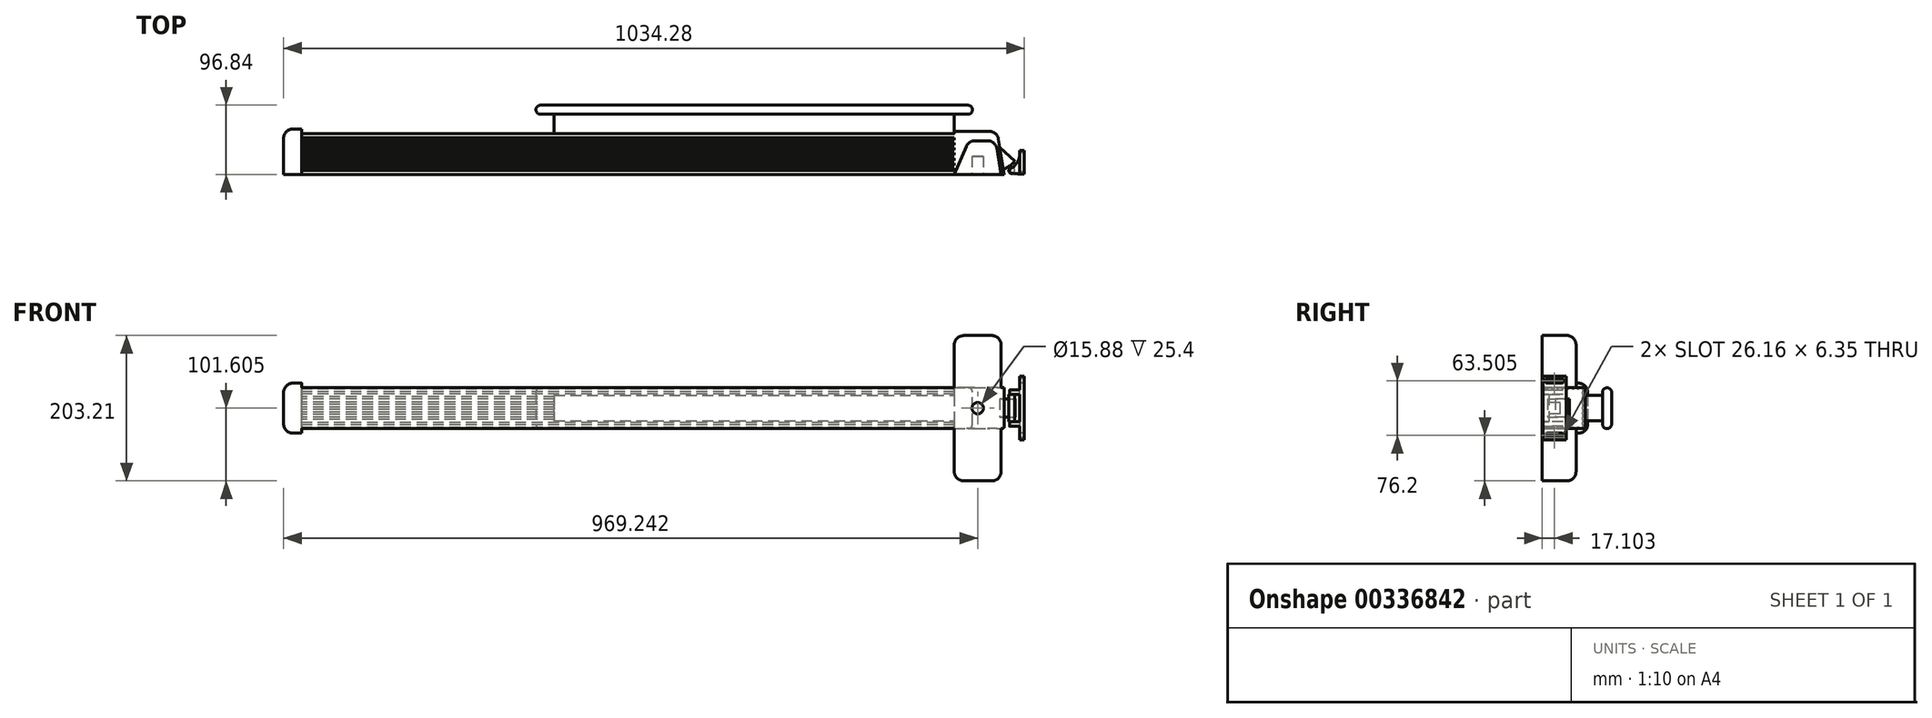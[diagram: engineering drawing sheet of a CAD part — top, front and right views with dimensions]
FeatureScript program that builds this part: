
annotation { "Feature Type Name" : "Feature", "Feature Type Description" : "" }
export const myFeature = defineFeature(function(context is Context, id is Id, definition is map)
    precondition{}
    {
        {
            var Q0;
            Q0=qCreatedBy(makeId("Front.planeOp"),FACE);
            var sketch = newSketch(context, id + "F0", { "sketchPlane" : qUnion([Q0])});
            skLineSegment(sketch, "E0.bottom", {"start": v(0, 0) * mm, "end": v(-911.23, 0) * mm});
            skLineSegment(sketch, "E0.top", {"start": v(0, 57.15) * mm, "end": v(-911.23, 57.15) * mm});
            skLineSegment(sketch, "E0.left", {"start": v(0, 0) * mm, "end": v(0, 57.15) * mm});
            skLineSegment(sketch, "E0.right", {"start": v(-911.23, 0) * mm, "end": v(-911.23, 57.15) * mm});
            skSolve(sketch);
        }
        {
            var Q0;
            Q0 = qSketchRegion(id + "F0", true);
            extrude(context, id + "F1", {"entities" : qUnion([Q0]), "oppositeDirection" : true, "depth" : 57.15 * mm});
        }
        {
            var Q0;
            Q0=qCreatedBy(makeId("Top.planeOp"),FACE);
            var sketch = newSketch(context, id + "F2", { "sketchPlane" : qUnion([Q0])});
            skLineSegment(sketch, "E1.bottom", {"start": v(0, 0) * mm, "end": v(69.85, 0) * mm});
            skLineSegment(sketch, "E1.left", {"start": v(0, 0) * mm, "end": v(0, 60.32) * mm});
            skLineSegment(sketch, "E2", {"start": v(0, 60.32) * mm, "end": v(49.18, 60.32) * mm});
            skLineSegment(sketch, "E3", {"start": v(61.72, 49.68) * mm, "end": v(69.85, 0) * mm});
            skPoint(sketch, "E4.visualSharp", {"position": v(59.97, 60.32) * mm});
            skArc(sketch, "E4.filletArc", {"start": v(61.72, 49.68) * mm, "mid": v(57.4, 57.3) * mm, "end": v(49.18, 60.33) * mm});
            skSolve(sketch);
        }
        {
            var Q0;
            Q0 = qSketchRegion(id + "F2", true);
            var Q1;
            Q1=makeQuery(id+"F1.opExtrude","SWEPT_FACE",FACE,{"disambiguationData":[OSD([sQuery(id+"F0.wireOp",EDGE,"E0.top")])]});
            extrude(context, id + "F3", {"entities" : qUnion([Q0]), "operationType" : NewBodyOperationType.ADD, "endBound" : BoundingType.UP_TO_SURFACE, "endBoundEntityFace" : qUnion([Q1]), "depth" : 25.4 * mm});
        }
        {
            var Q0;
            Q0=qCreatedBy(makeId("Top.planeOp"),FACE);
            var sketch = newSketch(context, id + "F4", { "sketchPlane" : qUnion([Q0])});
            skLineSegment(sketch, "E5", {"start": v(65.24, 0) * mm, "end": v(59.26, 36.55) * mm});
            skLineSegment(sketch, "E6", {"start": v(46.73, 47.2) * mm, "end": v(28.53, 47.2) * mm});
            skLineSegment(sketch, "E7", {"start": v(16.85, 39.48) * mm, "end": v(0, 0) * mm});
            skLineSegment(sketch, "E8", {"start": v(0, 0) * mm, "end": v(65.24, 0) * mm});
            skPoint(sketch, "E9.visualSharp", {"position": v(57.52, 47.2) * mm});
            skArc(sketch, "E9.filletArc", {"start": v(59.26, 36.55) * mm, "mid": v(54.95, 44.18) * mm, "end": v(46.73, 47.2) * mm});
            skPoint(sketch, "E10.visualSharp", {"position": v(20.14, 47.2) * mm});
            skArc(sketch, "E10.filletArc", {"start": v(28.53, 47.2) * mm, "mid": v(21.53, 45.1) * mm, "end": v(16.85, 39.48) * mm});
            skSolve(sketch);
        }
        {
            var Q0;
            Q0=makeQuery(id+"F3.opExtrude","CAP_EDGE",EDGE,{"disambiguationData":[OSD([sQuery(id+"F2.wireOp",EDGE,"E2")])],"isStart":true});
            var Q1;
            Q1=makeQuery(id+"F3.opExtrude","TWEAK_EDGE",EDGE,{"derivedFrom":[makeQuery(id+"F1.opExtrude","SWEPT_FACE",FACE,{"disambiguationData":[OSD([sQuery(id+"F0.wireOp",EDGE,"E0.top")])]}),makeQuery(id+"F2.imprint","IMPRINT",EDGE,{"derivedFrom":sQuery(id+"F2.wireOp",EDGE,"E2")})]});
            fillet(context, id + "F5", {"entities" : qUnion([Q0, Q1]), "radius" : 3.17 * mm, "tangentPropagation" : true, "allowEdgeOverflow" : false});
        }
        {
            var Q0;
            Q0 = qSketchRegion(id + "F4", true);
            extrude(context, id + "F6", {"entities" : qUnion([Q0]), "operationType" : NewBodyOperationType.ADD, "depth" : 130.17 * mm, "hasSecondDirection" : true, "secondDirectionOppositeDirection" : true, "secondDirectionDepth" : 73.02 * mm});
        }
        {
            var Q0;
            Q0=makeQuery(id+"F6.opExtrude","CAP_EDGE",EDGE,{"disambiguationData":[OSD([sQuery(id+"F4.wireOp",EDGE,"E7")])],"isStart":false});
            var Q1;
            Q1=makeQuery(id+"F6.opExtrude","CAP_EDGE",EDGE,{"disambiguationData":[OSD([sQuery(id+"F4.wireOp",EDGE,"E7")])],"isStart":true});
            fillet(context, id + "F7", {"entities" : qUnion([Q0, Q1]), "radius" : 12.7 * mm, "tangentPropagation" : true, "allowEdgeOverflow" : false});
        }
        {
            var Q0;
            Q0=makeQuery(id+"F1.opExtrude","SWEPT_FACE",FACE,{"disambiguationData":[OSD([sQuery(id+"F0.wireOp",EDGE,"E0.right")])]});
            var sketch = newSketch(context, id + "F8", { "sketchPlane" : qUnion([Q0])});
            skArc(sketch, "E11", {"start": v(-48.42, 0) * mm, "mid": v(-50, 1.59) * mm, "end": v(-51.6, 0) * mm});
            skArc(sketch, "E12.1.0.0", {"start": v(-41.28, 0) * mm, "mid": v(-42.86, 1.59) * mm, "end": v(-44.45, 0) * mm});
            skArc(sketch, "E12.2.0.0", {"start": v(-34.13, 0) * mm, "mid": v(-35.72, 1.59) * mm, "end": v(-37.3, 0) * mm});
            skArc(sketch, "E12.3.0.0", {"start": v(-26.99, 0) * mm, "mid": v(-28.57, 1.59) * mm, "end": v(-30.16, 0) * mm});
            skArc(sketch, "E12.4.0.0", {"start": v(-19.84, 0) * mm, "mid": v(-21.43, 1.59) * mm, "end": v(-23.02, 0) * mm});
            skArc(sketch, "E12.5.0.0", {"start": v(-12.7, 0) * mm, "mid": v(-14.29, 1.59) * mm, "end": v(-15.87, 0) * mm});
            skArc(sketch, "E12.6.0.0", {"start": v(-5.56, 0) * mm, "mid": v(-7.14, 1.59) * mm, "end": v(-8.73, 0) * mm});
            skLineSegment(sketch, "E12.direction1", {"start": v(-51.6, 0) * mm, "end": v(-44.45, 0) * mm, "construction": true});
            skLineSegment(sketch, "E13", {"start": v(-50, 7.14) * mm, "end": v(-57.15, 7.14) * mm, "construction": true});
            skPoint(sketch, "E13.startSnap0", {"position": v(-50, 1.59) * mm});
            skLineSegment(sketch, "E14", {"start": v(-50, 7.14) * mm, "end": v(-50, 0) * mm, "construction": true});
            skLineSegment(sketch, "E15.0", {"start": v(-57.15, 0) * mm, "end": v(-57.15, 57.15) * mm, "construction": true});
            skLineSegment(sketch, "E16", {"start": v(-57.15, 28.58) * mm, "end": v(0, 28.58) * mm, "construction": true});
            skArc(sketch, "E17.1.0", {"start": v(-57.15, 5.56) * mm, "mid": v(-55.56, 7.14) * mm, "end": v(-57.15, 8.73) * mm});
            skPoint(sketch, "E17.center", {"position": v(-50, 7.14) * mm});
            skLineSegment(sketch, "E17.anchor1", {"start": v(-50, 7.14) * mm, "end": v(-51.6, 0) * mm, "construction": true});
            skLineSegment(sketch, "E17.anchor2", {"start": v(-50, 7.14) * mm, "end": v(-57.15, 8.73) * mm, "construction": true});
            skArc(sketch, "E18.MirrorCS", {"start": v(-48.42, 57.15) * mm, "mid": v(-50, 55.56) * mm, "end": v(-51.6, 57.15) * mm});
            skPoint(sketch, "E19.MirrorP", {"position": v(-50, 55.56) * mm});
            skArc(sketch, "E20.MirrorCS", {"start": v(-34.13, 57.15) * mm, "mid": v(-35.72, 55.56) * mm, "end": v(-37.3, 57.15) * mm});
            skArc(sketch, "E21.MirrorCS", {"start": v(-41.28, 57.15) * mm, "mid": v(-42.86, 55.56) * mm, "end": v(-44.45, 57.15) * mm});
            skArc(sketch, "E22.MirrorCS", {"start": v(-26.99, 57.15) * mm, "mid": v(-28.57, 55.56) * mm, "end": v(-30.16, 57.15) * mm});
            skArc(sketch, "E23.MirrorCS", {"start": v(-5.56, 57.15) * mm, "mid": v(-7.14, 55.56) * mm, "end": v(-8.73, 57.15) * mm});
            skLineSegment(sketch, "E24.MirrorCS", {"start": v(-51.6, 57.15) * mm, "end": v(-44.45, 57.15) * mm, "construction": true});
            skArc(sketch, "E25.MirrorCS", {"start": v(-19.84, 57.15) * mm, "mid": v(-21.43, 55.56) * mm, "end": v(-23.02, 57.15) * mm});
            skArc(sketch, "E26.MirrorCS", {"start": v(-12.7, 57.15) * mm, "mid": v(-14.29, 55.56) * mm, "end": v(-15.87, 57.15) * mm});
            skLineSegment(sketch, "E27", {"start": v(-51.6, 0) * mm, "end": v(-48.42, 0) * mm});
            skLineSegment(sketch, "E28", {"start": v(-44.45, 0) * mm, "end": v(-41.28, 0) * mm});
            skLineSegment(sketch, "E29", {"start": v(-37.3, 0) * mm, "end": v(-34.13, 0) * mm});
            skLineSegment(sketch, "E30", {"start": v(-30.16, 0) * mm, "end": v(-26.99, 0) * mm});
            skLineSegment(sketch, "E31", {"start": v(-23.02, 0) * mm, "end": v(-19.84, 0) * mm});
            skLineSegment(sketch, "E32", {"start": v(-15.87, 0) * mm, "end": v(-12.7, 0) * mm});
            skLineSegment(sketch, "E33", {"start": v(-8.73, 0) * mm, "end": v(-5.56, 0) * mm});
            skLineSegment(sketch, "E34", {"start": v(-5.56, 57.15) * mm, "end": v(-8.73, 57.15) * mm});
            skLineSegment(sketch, "E35", {"start": v(-12.7, 57.15) * mm, "end": v(-15.87, 57.15) * mm});
            skLineSegment(sketch, "E36", {"start": v(-19.84, 57.15) * mm, "end": v(-23.02, 57.15) * mm});
            skLineSegment(sketch, "E37", {"start": v(-26.99, 57.15) * mm, "end": v(-30.16, 57.15) * mm});
            skLineSegment(sketch, "E38", {"start": v(-34.13, 57.15) * mm, "end": v(-37.3, 57.15) * mm});
            skLineSegment(sketch, "E39", {"start": v(-41.28, 57.15) * mm, "end": v(-44.45, 57.15) * mm});
            skLineSegment(sketch, "E40", {"start": v(-48.42, 57.15) * mm, "end": v(-51.6, 57.15) * mm});
            skLineSegment(sketch, "E41", {"start": v(-57.15, 5.56) * mm, "end": v(-57.15, 8.73) * mm});
            skArc(sketch, "E42.0.1.0", {"start": v(-57.15, 12.7) * mm, "mid": v(-55.56, 14.29) * mm, "end": v(-57.15, 15.88) * mm});
            skLineSegment(sketch, "E42.0.1.1", {"start": v(-57.15, 12.7) * mm, "end": v(-57.15, 15.88) * mm});
            skArc(sketch, "E42.0.2.0", {"start": v(-57.15, 19.84) * mm, "mid": v(-55.56, 21.43) * mm, "end": v(-57.15, 23.02) * mm});
            skLineSegment(sketch, "E42.0.2.1", {"start": v(-57.15, 19.84) * mm, "end": v(-57.15, 23.02) * mm});
            skArc(sketch, "E42.0.3.0", {"start": v(-57.15, 26.99) * mm, "mid": v(-55.56, 28.58) * mm, "end": v(-57.15, 30.16) * mm});
            skLineSegment(sketch, "E42.0.3.1", {"start": v(-57.15, 26.99) * mm, "end": v(-57.15, 30.16) * mm});
            skArc(sketch, "E42.0.4.0", {"start": v(-57.15, 34.13) * mm, "mid": v(-55.56, 35.72) * mm, "end": v(-57.15, 37.3) * mm});
            skLineSegment(sketch, "E42.0.4.1", {"start": v(-57.15, 34.13) * mm, "end": v(-57.15, 37.3) * mm});
            skArc(sketch, "E42.0.5.0", {"start": v(-57.15, 41.28) * mm, "mid": v(-55.56, 42.86) * mm, "end": v(-57.15, 44.45) * mm});
            skLineSegment(sketch, "E42.0.5.1", {"start": v(-57.15, 41.28) * mm, "end": v(-57.15, 44.45) * mm});
            skArc(sketch, "E42.0.6.0", {"start": v(-57.15, 48.42) * mm, "mid": v(-55.56, 50) * mm, "end": v(-57.15, 51.6) * mm});
            skLineSegment(sketch, "E42.0.6.1", {"start": v(-57.15, 48.42) * mm, "end": v(-57.15, 51.6) * mm});
            skLineSegment(sketch, "E42.direction1", {"start": v(-57.15, 5.56) * mm, "end": v(-31.75, 5.56) * mm, "construction": true});
            skLineSegment(sketch, "E42.direction2", {"start": v(-57.15, 5.56) * mm, "end": v(-57.15, 12.7) * mm, "construction": true});
            skSolve(sketch);
        }
        {
            var Q0;
            Q0 = qSketchRegion(id + "F8", true);
            var Q1;
            Q1=makeQuery(id+"F3.opExtrude","SWEPT_FACE",FACE,{"disambiguationData":[OSD([sQuery(id+"F2.wireOp",EDGE,"E1.left")])]});
            extrude(context, id + "F9", {"entities" : qUnion([Q0]), "operationType" : NewBodyOperationType.REMOVE, "endBound" : BoundingType.UP_TO_SURFACE, "oppositeDirection" : true, "endBoundEntityFace" : qUnion([Q1]), "depth" : 25.4 * mm});
        }
        {
            var Q0;
            Q0=makeQuery(id+"F1.opExtrude","SWEPT_FACE",FACE,{"disambiguationData":[OSD([sQuery(id+"F0.wireOp",EDGE,"E0.right")])]});
            var sketch = newSketch(context, id + "F10", { "sketchPlane" : qUnion([Q0])});
            skLineSegment(sketch, "E43.bottom", {"start": v(0, 63.5) * mm, "end": v(-63.5, 63.5) * mm});
            skLineSegment(sketch, "E43.top", {"start": v(0, -6.35) * mm, "end": v(-63.5, -6.35) * mm});
            skLineSegment(sketch, "E43.left", {"start": v(0, 63.5) * mm, "end": v(0, -6.35) * mm});
            skLineSegment(sketch, "E43.right", {"start": v(-63.5, 63.5) * mm, "end": v(-63.5, -6.35) * mm});
            skSolve(sketch);
        }
        {
            var Q0;
            Q0 = qSketchRegion(id + "F10", true);
            extrude(context, id + "F11", {"entities" : qUnion([Q0]), "operationType" : NewBodyOperationType.ADD, "depth" : 25.4 * mm});
        }
        {
            var Q0;
            Q0=makeQuery(id+"F11.opExtrude","SWEPT_EDGE",EDGE,{"disambiguationData":[OSD([sQuery(id+"F10.wireOp",EDGE,"E43.top"),sQuery(id+"F10.wireOp",EDGE,"E43.right")])]});
            var Q1;
            Q1=makeQuery(id+"F11.opExtrude","SWEPT_EDGE",EDGE,{"disambiguationData":[OSD([sQuery(id+"F10.wireOp",EDGE,"E43.bottom"),sQuery(id+"F10.wireOp",EDGE,"E43.right")])]});
            fillet(context, id + "F12", {"entities" : qUnion([Q0, Q1]), "radius" : 12.7 * mm, "tangentPropagation" : true, "allowEdgeOverflow" : false});
        }
        {
            var Q0;
            Q0=makeQuery(id+"F11.opExtrude","CAP_EDGE",EDGE,{"disambiguationData":[OSD([sQuery(id+"F10.wireOp",EDGE,"E43.bottom")])],"isStart":false});
            fillet(context, id + "F13", {"entities" : qUnion([Q0]), "radius" : 12.7 * mm, "tangentPropagation" : true, "allowEdgeOverflow" : false});
        }
        {
            var Q0;
            {var subQ0=sQuery(id+"F2.wireOp",EDGE,"E1.left");var subQ1=sQuery(id+"F8.wireOp",EDGE,"E42.0.6.0");var subQ2=sQuery(id+"F0.wireOp",EDGE,"E0.top");var subQ3=sQuery(id+"F0.wireOp",EDGE,"E0.right");Q0=makeQuery(id+"F9.boolean.opBoolean","SPLIT",FACE,{"disambiguationData":[TD([makeQuery(id+"F1.opExtrude","SWEPT_FACE",FACE,{"disambiguationData":[OSD([subQ2])]}),makeQuery(id+"F1.opExtrude","SWEPT_FACE",FACE,{"disambiguationData":[OSD([subQ3])]}),makeQuery(id+"F3.opExtrude","CAP_FACE",FACE,{"disambiguationData":[OSD([subQ2])],"isStart":false}),makeQuery(id+"F3.opExtrude","SWEPT_FACE",FACE,{"disambiguationData":[OSD([subQ0])]}),makeQuery(id+"F5.opFillet","BLEND_FACE",FACE,{"disambiguationData":[OSD([subQ2,sQuery(id+"F2.wireOp",EDGE,"E2")])]}),makeQuery(id+"F9.opExtrude","SWEPT_FACE",FACE,{"disambiguationData":[OSD([subQ1])]}),makeQuery(id+"F9.opExtrude","CAP_FACE",FACE,{"disambiguationData":[OSD([subQ0]),ownerDisambiguation([makeQuery(id+"F9.opExtrude","SWEPT_BODY",BODY,{"disambiguationData":[OSD([sQuery(id+"F8.wireOp",EDGE,"E17.1.0"),sQuery(id+"F8.wireOp",EDGE,"E41")])]})])],"isStart":false}),makeQuery(id+"F9.opExtrude","CAP_FACE",FACE,{"disambiguationData":[OSD([subQ0]),ownerDisambiguation([makeQuery(id+"F9.opExtrude","SWEPT_BODY",BODY,{"disambiguationData":[OSD([sQuery(id+"F8.wireOp",EDGE,"E42.0.1.0"),sQuery(id+"F8.wireOp",EDGE,"E42.0.1.1")])]})])],"isStart":false}),makeQuery(id+"F9.opExtrude","CAP_FACE",FACE,{"disambiguationData":[OSD([subQ0]),ownerDisambiguation([makeQuery(id+"F9.opExtrude","SWEPT_BODY",BODY,{"disambiguationData":[OSD([sQuery(id+"F8.wireOp",EDGE,"E42.0.2.0"),sQuery(id+"F8.wireOp",EDGE,"E42.0.2.1")])]})])],"isStart":false}),makeQuery(id+"F9.opExtrude","CAP_FACE",FACE,{"disambiguationData":[OSD([subQ0]),ownerDisambiguation([makeQuery(id+"F9.opExtrude","SWEPT_BODY",BODY,{"disambiguationData":[OSD([sQuery(id+"F8.wireOp",EDGE,"E42.0.3.0"),sQuery(id+"F8.wireOp",EDGE,"E42.0.3.1")])]})])],"isStart":false}),makeQuery(id+"F9.opExtrude","CAP_FACE",FACE,{"disambiguationData":[OSD([subQ0]),ownerDisambiguation([makeQuery(id+"F9.opExtrude","SWEPT_BODY",BODY,{"disambiguationData":[OSD([sQuery(id+"F8.wireOp",EDGE,"E42.0.4.0"),sQuery(id+"F8.wireOp",EDGE,"E42.0.4.1")])]})])],"isStart":false}),makeQuery(id+"F9.opExtrude","CAP_FACE",FACE,{"disambiguationData":[OSD([subQ0]),ownerDisambiguation([makeQuery(id+"F9.opExtrude","SWEPT_BODY",BODY,{"disambiguationData":[OSD([sQuery(id+"F8.wireOp",EDGE,"E42.0.5.0"),sQuery(id+"F8.wireOp",EDGE,"E42.0.5.1")])]})])],"isStart":false}),makeQuery(id+"F9.opExtrude","CAP_FACE",FACE,{"disambiguationData":[OSD([subQ0]),ownerDisambiguation([makeQuery(id+"F9.opExtrude","SWEPT_BODY",BODY,{"disambiguationData":[OSD([subQ1,sQuery(id+"F8.wireOp",EDGE,"E42.0.6.1")])]})])],"isStart":false})])],"derivedFrom":makeQuery(id+"F1.opExtrude","CAP_FACE",FACE,{"disambiguationData":[OSD([sQuery(id+"F0.wireOp",EDGE,"E0.bottom"),subQ2,sQuery(id+"F0.wireOp",EDGE,"E0.left"),subQ3])],"isStart":false})});}
            var sketch = newSketch(context, id + "F14", { "sketchPlane" : qUnion([Q0])});
            skPoint(sketch, "E44.0", {"position": v(0, 46.43) * mm});
            skPoint(sketch, "E45.0", {"position": v(0, 10.72) * mm});
            skLineSegment(sketch, "E46.bottom", {"start": v(0, 46.43) * mm, "end": v(558.8, 46.43) * mm});
            skLineSegment(sketch, "E46.top", {"start": v(0, 10.72) * mm, "end": v(558.8, 10.72) * mm});
            skLineSegment(sketch, "E46.left", {"start": v(0, 46.43) * mm, "end": v(0, 10.72) * mm});
            skLineSegment(sketch, "E46.right", {"start": v(558.8, 46.43) * mm, "end": v(558.8, 10.72) * mm});
            skSolve(sketch);
        }
        {
            var Q0;
            Q0 = qSketchRegion(id + "F14", true);
            extrude(context, id + "F15", {"entities" : qUnion([Q0]), "operationType" : NewBodyOperationType.ADD, "oppositeDirection" : true, "depth" : 25.4 * mm, "hasSecondDirection" : true, "secondDirectionOppositeDirection" : false, "secondDirectionDepth" : 26.99 * mm});
        }
        {
            var Q0;
            Q0=makeQuery(id+"F15.opExtrude","CAP_FACE",FACE,{"disambiguationData":[OSD([sQuery(id+"F14.wireOp",EDGE,"E46.bottom"),sQuery(id+"F14.wireOp",EDGE,"E46.top"),sQuery(id+"F14.wireOp",EDGE,"E46.left"),sQuery(id+"F14.wireOp",EDGE,"E46.right")])],"isStart":true});
            var sketch = newSketch(context, id + "F16", { "sketchPlane" : qUnion([Q0])});
            skLineSegment(sketch, "E47.bottom", {"start": v(-25.4, 57.15) * mm, "end": v(584.2, 57.15) * mm});
            skLineSegment(sketch, "E47.top", {"start": v(-25.4, 0) * mm, "end": v(584.2, 0) * mm});
            skLineSegment(sketch, "E47.left", {"start": v(-25.4, 57.15) * mm, "end": v(-25.4, 0) * mm});
            skLineSegment(sketch, "E47.right", {"start": v(584.2, 57.15) * mm, "end": v(584.2, 0) * mm});
            skSolve(sketch);
        }
        {
            var Q0;
            Q0 = qSketchRegion(id + "F16", true);
            extrude(context, id + "F17", {"entities" : qUnion([Q0]), "operationType" : NewBodyOperationType.ADD, "depth" : 12.7 * mm});
        }
        {
            var Q0;
            Q0=makeQuery(id+"F17.opExtrude","CAP_EDGE",EDGE,{"disambiguationData":[OSD([sQuery(id+"F16.wireOp",EDGE,"E47.bottom")])],"isStart":false});
            var Q1;
            Q1=makeQuery(id+"F17.opExtrude","CAP_EDGE",EDGE,{"disambiguationData":[OSD([sQuery(id+"F16.wireOp",EDGE,"E47.left")])],"isStart":false});
            var Q2;
            Q2=makeQuery(id+"F17.opExtrude","CAP_EDGE",EDGE,{"disambiguationData":[OSD([sQuery(id+"F16.wireOp",EDGE,"E47.top")])],"isStart":false});
            var Q3;
            Q3=makeQuery(id+"F17.opExtrude","CAP_EDGE",EDGE,{"disambiguationData":[OSD([sQuery(id+"F16.wireOp",EDGE,"E47.top")])],"isStart":true});
            var Q4;
            Q4=makeQuery(id+"F17.opExtrude","CAP_EDGE",EDGE,{"disambiguationData":[OSD([sQuery(id+"F16.wireOp",EDGE,"E47.left")])],"isStart":true});
            var Q5;
            Q5=makeQuery(id+"F17.opExtrude","SWEPT_EDGE",EDGE,{"disambiguationData":[OSD([sQuery(id+"F16.wireOp",EDGE,"E47.top"),sQuery(id+"F16.wireOp",EDGE,"E47.left")])]});
            var Q6;
            Q6=makeQuery(id+"F17.opExtrude","SWEPT_EDGE",EDGE,{"disambiguationData":[OSD([sQuery(id+"F16.wireOp",EDGE,"E47.bottom"),sQuery(id+"F16.wireOp",EDGE,"E47.left")])]});
            var Q7;
            Q7=makeQuery(id+"F17.opExtrude","CAP_EDGE",EDGE,{"disambiguationData":[OSD([sQuery(id+"F16.wireOp",EDGE,"E47.right")])],"isStart":true});
            var Q8;
            Q8=makeQuery(id+"F17.opExtrude","CAP_EDGE",EDGE,{"disambiguationData":[OSD([sQuery(id+"F16.wireOp",EDGE,"E47.right")])],"isStart":false});
            var Q9;
            Q9=makeQuery(id+"F17.opExtrude","SWEPT_EDGE",EDGE,{"disambiguationData":[OSD([sQuery(id+"F16.wireOp",EDGE,"E47.top"),sQuery(id+"F16.wireOp",EDGE,"E47.right")])]});
            var Q10;
            Q10=makeQuery(id+"F17.opExtrude","SWEPT_EDGE",EDGE,{"disambiguationData":[OSD([sQuery(id+"F16.wireOp",EDGE,"E47.bottom"),sQuery(id+"F16.wireOp",EDGE,"E47.right")])]});
            var Q11;
            Q11=makeQuery(id+"F17.opExtrude","CAP_EDGE",EDGE,{"disambiguationData":[OSD([sQuery(id+"F16.wireOp",EDGE,"E47.bottom")])],"isStart":true});
            fillet(context, id + "F18", {"entities" : qUnion([Q0, Q1, Q2, Q3, Q4, Q5, Q6, Q7, Q8, Q9, Q10, Q11]), "radius" : 6.35 * mm, "tangentPropagation" : true, "allowEdgeOverflow" : false});
        }
        {
            var Q0;
            Q0=makeQuery(id+"F11.boolean.opBoolean","MERGE",FACE,{"derivedFrom":[makeQuery(id+"F6.boolean.opBoolean","MERGE",FACE,{"derivedFrom":[makeQuery(id+"F3.boolean.opBoolean","MERGE",FACE,{"derivedFrom":[makeQuery(id+"F1.opExtrude","CAP_FACE",FACE,{"disambiguationData":[OSD([sQuery(id+"F0.wireOp",EDGE,"E0.bottom"),sQuery(id+"F0.wireOp",EDGE,"E0.top"),sQuery(id+"F0.wireOp",EDGE,"E0.left"),sQuery(id+"F0.wireOp",EDGE,"E0.right")])],"isStart":true}),makeQuery(id+"F3.opExtrude","SWEPT_FACE",FACE,{"disambiguationData":[OSD([sQuery(id+"F2.wireOp",EDGE,"E1.bottom")])]})]}),makeQuery(id+"F6.opExtrude","SWEPT_FACE",FACE,{"disambiguationData":[OSD([sQuery(id+"F4.wireOp",EDGE,"E8")])]})]}),makeQuery(id+"F11.opExtrude","SWEPT_FACE",FACE,{"disambiguationData":[OSD([sQuery(id+"F10.wireOp",EDGE,"E43.left")])]})]});
            var sketch = newSketch(context, id + "F19", { "sketchPlane" : qUnion([Q0])});
            skPoint(sketch, "E48.0", {"position": v(0, 117.48) * mm});
            skPoint(sketch, "E49.0", {"position": v(65.24, -60.32) * mm});
            skLineSegment(sketch, "E50", {"start": v(0, 117.48) * mm, "end": v(65.24, -60.33) * mm, "construction": true});
            skCircle(sketch, "E51", {"center": v(32.62, 28.58) * mm, "radius": 7.94 * mm});
            skSolve(sketch);
        }
        {
            var Q0;
            Q0 = qSketchRegion(id + "F19", true);
            extrude(context, id + "F20", {"entities" : qUnion([Q0]), "operationType" : NewBodyOperationType.REMOVE, "oppositeDirection" : true, "depth" : 25.4 * mm});
        }
        {
            var Q0;
            Q0=qCreatedBy(makeId("Front.planeOp"),FACE);
            var sketch = newSketch(context, id + "F21", { "sketchPlane" : qUnion([Q0])});
            skPoint(sketch, "E52.0", {"position": v(69.85, 28.58) * mm});
            skSolve(sketch);
        }
        {
            var Q0;
            Q0=qCreatedBy(makeId("Top.planeOp"),FACE);
            var Q1;
            Q1=sQuery(id+"F21.wireOp",VERTEX,"E52.0");
            cPlane(context, id + "F22", {"entities" : qUnion([Q0, Q1]), "cplaneType" : CPlaneType.PLANE_POINT, "offset" : 25.4 * mm, "width" : 152.4 * mm, "height" : 152.4 * mm});
        }
        {
            var Q0;
            Q0=qCreatedBy(id+"F22.planeOp",FACE);
            var sketch = newSketch(context, id + "F23", { "sketchPlane" : qUnion([Q0])});
            skLineSegment(sketch, "E53.0", {"start": v(61.72, 49.68) * mm, "end": v(69.85, 0) * mm, "construction": true});
            skLineSegment(sketch, "E54", {"start": v(63.63, 38) * mm, "end": v(84.7, 18.4) * mm});
            skLineSegment(sketch, "E55", {"start": v(84.7, 18.4) * mm, "end": v(95.06, 29.56) * mm, "construction": true});
            skArc(sketch, "E56", {"start": v(84.7, 18.4) * mm, "mid": v(77.28, 12) * mm, "end": v(68.65, 7.35) * mm});
            skLineSegment(sketch, "E57", {"start": v(68.65, 7.35) * mm, "end": v(63.63, 38) * mm});
            skSolve(sketch);
        }
        {
            var Q0;
            Q0 = qSketchRegion(id + "F23", true);
            extrude(context, id + "F24", {"entities" : qUnion([Q0]), "operationType" : NewBodyOperationType.ADD, "depth" : 12.7 * mm, "hasSecondDirection" : true, "secondDirectionOppositeDirection" : true, "secondDirectionDepth" : 12.7 * mm});
        }
        {
            var Q0;
            Q0=qCreatedBy(id+"F22.planeOp",FACE);
            var sketch = newSketch(context, id + "F25", { "sketchPlane" : qUnion([Q0])});
            skCircle(sketch, "E58", {"center": v(80.35, 5.47) * mm, "radius": 4.15 * mm});
            skCircle(sketch, "E59.0", {"center": v(80.35, 5.47) * mm, "radius": 3.34 * mm, "construction": true});
            skLineSegment(sketch, "E60.bottom", {"start": v(97.66, 33.36) * mm, "end": v(91.38, 33.36) * mm});
            skLineSegment(sketch, "E60.top", {"start": v(97.66, 0.85) * mm, "end": v(91.38, 0.85) * mm});
            skLineSegment(sketch, "E60.left", {"start": v(97.66, 33.36) * mm, "end": v(97.66, 0.85) * mm});
            skLineSegment(sketch, "E60.right", {"start": v(91.38, 33.36) * mm, "end": v(91.38, 0.85) * mm});
            skArc(sketch, "E61", {"start": v(91.38, 0.85) * mm, "mid": v(85.44, 1.2) * mm, "end": v(79.59, 2.22) * mm});
            skLineSegment(sketch, "E62", {"start": v(91.38, 33.36) * mm, "end": v(91.38, 28.84) * mm, "construction": true});
            skArc(sketch, "E63", {"start": v(91.38, 28.84) * mm, "mid": v(88, 16.87) * mm, "end": v(78.85, 8.45) * mm});
            skArc(sketch, "E64", {"start": v(78.85, 8.45) * mm, "mid": v(77.04, 5.07) * mm, "end": v(79.59, 2.22) * mm});
            skSolve(sketch);
        }
        {
            var Q0;
            {var subQ1=sQuery(id+"F25.wireOp",EDGE,"E60.bottom");Q0=makeQuery(id+"F25.imprint","IMPRINT",FACE,{"disambiguationData":[TD([[makeQuery(id+"F25.imprint","IMPRINT",EDGE,{"derivedFrom":subQ1}),1.0]])]});}
            extrude(context, id + "F26", {"entities" : qUnion([Q0]), "depth" : 25.4 * mm, "hasSecondDirection" : true, "secondDirectionOppositeDirection" : true, "secondDirectionDepth" : 25.4 * mm});
        }
        {
            var Q0;
            Q0=makeQuery(id+"F26.opExtrude","CAP_FACE",FACE,{"disambiguationData":[OSD([sQuery(id+"F25.wireOp",EDGE,"E60.bottom"),sQuery(id+"F25.wireOp",EDGE,"E60.top"),sQuery(id+"F25.wireOp",EDGE,"E60.left"),sQuery(id+"F25.wireOp",EDGE,"E60.right")])],"isStart":true});
            var sketch = newSketch(context, id + "F27", { "sketchPlane" : qUnion([Q0])});
            skArc(sketch, "E65.0.0", {"start": v(82.09, -1.7) * mm, "mid": v(86.71, -1.06) * mm, "end": v(91.38, -0.85) * mm});
            skLineSegment(sketch, "E65.0.1", {"start": v(91.38, -0.85) * mm, "end": v(91.38, -28.84) * mm});
            skArc(sketch, "E65.0.2", {"start": v(91.38, -28.84) * mm, "mid": v(88.57, -17.87) * mm, "end": v(80.85, -9.6) * mm});
            skArc(sketch, "E65.0.3", {"start": v(80.85, -9.6) * mm, "mid": v(84.46, -6.11) * mm, "end": v(82.09, -1.7) * mm});
            skArc(sketch, "E66.0.0", {"start": v(79.59, -2.22) * mm, "mid": v(80.83, -1.94) * mm, "end": v(82.09, -1.7) * mm});
            skArc(sketch, "E66.0.1", {"start": v(82.09, -1.7) * mm, "mid": v(84.46, -6.11) * mm, "end": v(80.85, -9.6) * mm});
            skArc(sketch, "E66.0.2", {"start": v(80.85, -9.6) * mm, "mid": v(79.86, -9) * mm, "end": v(78.85, -8.45) * mm});
            skArc(sketch, "E66.0.3", {"start": v(78.85, -8.45) * mm, "mid": v(77.04, -5.07) * mm, "end": v(79.59, -2.22) * mm});
            skSolve(sketch);
        }
        {
            var Q0;
            Q0=makeQuery(id+"F26.opExtrude","CAP_FACE",FACE,{"disambiguationData":[OSD([sQuery(id+"F25.wireOp",EDGE,"E60.bottom"),sQuery(id+"F25.wireOp",EDGE,"E60.top"),sQuery(id+"F25.wireOp",EDGE,"E60.left"),sQuery(id+"F25.wireOp",EDGE,"E60.right")])],"isStart":false});
            var sketch = newSketch(context, id + "F28", { "sketchPlane" : qUnion([Q0])});
            skArc(sketch, "E67.0.0", {"start": v(82.09, 1.7) * mm, "mid": v(86.71, 1.06) * mm, "end": v(91.38, 0.85) * mm});
            skLineSegment(sketch, "E67.0.1", {"start": v(91.38, 0.85) * mm, "end": v(91.38, 28.84) * mm});
            skArc(sketch, "E67.0.2", {"start": v(91.38, 28.84) * mm, "mid": v(88.57, 17.87) * mm, "end": v(80.85, 9.6) * mm});
            skArc(sketch, "E67.0.3", {"start": v(80.85, 9.6) * mm, "mid": v(84.46, 6.11) * mm, "end": v(82.09, 1.7) * mm});
            skArc(sketch, "E68.0.0", {"start": v(79.59, 2.22) * mm, "mid": v(80.83, 1.94) * mm, "end": v(82.09, 1.7) * mm});
            skArc(sketch, "E68.0.1", {"start": v(82.09, 1.7) * mm, "mid": v(84.46, 6.11) * mm, "end": v(80.85, 9.6) * mm});
            skArc(sketch, "E68.0.2", {"start": v(80.85, 9.6) * mm, "mid": v(79.86, 9) * mm, "end": v(78.85, 8.45) * mm});
            skArc(sketch, "E68.0.3", {"start": v(78.85, 8.45) * mm, "mid": v(77.04, 5.07) * mm, "end": v(79.59, 2.22) * mm});
            skSolve(sketch);
        }
        {
            var Q0;
            Q0 = qSketchRegion(id + "F27", true);
            extrude(context, id + "F29", {"entities" : qUnion([Q0]), "operationType" : NewBodyOperationType.ADD, "oppositeDirection" : true, "depth" : 6.35 * mm});
        }
        {
            var Q0;
            Q0 = qSketchRegion(id + "F28", true);
            extrude(context, id + "F30", {"entities" : qUnion([Q0]), "operationType" : NewBodyOperationType.ADD, "oppositeDirection" : true, "depth" : 6.35 * mm});
        }
        {
            var Q0;
            {var subQ5=sQuery(id+"F25.wireOp",EDGE,"E64");Q0=makeQuery(id+"F25.imprint","IMPRINT",FACE,{"disambiguationData":[TD([[makeQuery(id+"F25.imprint","IMPRINT",EDGE,{"derivedFrom":subQ5}),-1.0]])]});}
            var Q1;
            {var subQ5=sQuery(id+"F25.wireOp",EDGE,"E64");Q1=makeQuery(id+"F25.imprint","IMPRINT",FACE,{"disambiguationData":[TD([[makeQuery(id+"F25.imprint","IMPRINT",EDGE,{"derivedFrom":subQ5}),1.0]])]});}
            var Q2;
            Q2=makeQuery(id+"F30.opExtrude","CAP_FACE",FACE,{"disambiguationData":[OSD([sQuery(id+"F28.wireOp",EDGE,"E67.0.0"),sQuery(id+"F28.wireOp",EDGE,"E67.0.1"),sQuery(id+"F28.wireOp",EDGE,"E67.0.2"),sQuery(id+"F28.wireOp",EDGE,"E68.0.0"),sQuery(id+"F28.wireOp",EDGE,"E68.0.2"),sQuery(id+"F28.wireOp",EDGE,"E68.0.3")])],"isStart":false});
            var Q3;
            Q3=makeQuery(id+"F29.opExtrude","CAP_FACE",FACE,{"disambiguationData":[OSD([sQuery(id+"F27.wireOp",EDGE,"E65.0.0"),sQuery(id+"F27.wireOp",EDGE,"E65.0.1"),sQuery(id+"F27.wireOp",EDGE,"E65.0.2"),sQuery(id+"F27.wireOp",EDGE,"E66.0.0"),sQuery(id+"F27.wireOp",EDGE,"E66.0.2"),sQuery(id+"F27.wireOp",EDGE,"E66.0.3")])],"isStart":false});
            extrude(context, id + "F31", {"entities" : qUnion([Q0, Q1]), "operationType" : NewBodyOperationType.ADD, "endBound" : BoundingType.UP_TO_SURFACE, "endBoundEntityFace" : qUnion([Q2]), "depth" : 25.4 * mm, "hasSecondDirection" : true, "secondDirectionBound" : SecondDirectionBoundingType.UP_TO_SURFACE, "secondDirectionOppositeDirection" : true, "secondDirectionBoundEntityFace" : qUnion([Q3]), "secondDirectionDepth" : 25.4 * mm});
        }
        {
            var Q0;
            {var subQ1=sQuery(id+"F25.wireOp",EDGE,"E60.bottom");Q0=makeQuery(id+"F25.imprint","IMPRINT",FACE,{"disambiguationData":[TD([[makeQuery(id+"F25.imprint","IMPRINT",EDGE,{"derivedFrom":subQ1}),1.0]])]});}
            extrude(context, id + "F32", {"entities" : qUnion([Q0]), "operationType" : NewBodyOperationType.ADD, "depth" : 44.45 * mm, "hasSecondDirection" : true, "secondDirectionOppositeDirection" : true, "secondDirectionDepth" : 44.45 * mm});
        }
        {
            var Q0;
            {var subQ0=sQuery(id+"F25.wireOp",EDGE,"E60.right");Q0=makeQuery(id+"F32.boolean.opBoolean","MERGE",FACE,{"derivedFrom":[makeQuery(id+"F26.opExtrude","SWEPT_FACE",FACE,{"disambiguationData":[OSD([subQ0])]}),makeQuery(id+"F32.opExtrude","SWEPT_FACE",FACE,{"disambiguationData":[OSD([subQ0])]})]});}
            var sketch = newSketch(context, id + "F33", { "sketchPlane" : qUnion([Q0])});
            skLineSegment(sketch, "E69", {"start": v(-7.2, -12.7) * mm, "end": v(-27, -12.7) * mm});
            skLineSegment(sketch, "E70", {"start": v(-7.2, -6.35) * mm, "end": v(-27, -6.35) * mm});
            skArc(sketch, "E71", {"start": v(-7.2, -12.7) * mm, "mid": v(-4.02, -9.52) * mm, "end": v(-7.2, -6.35) * mm});
            skArc(sketch, "E72", {"start": v(-27, -6.35) * mm, "mid": v(-30.18, -9.52) * mm, "end": v(-27, -12.7) * mm});
            skLineSegment(sketch, "E73", {"start": v(-33.36, 28.58) * mm, "end": v(-0.85, 28.58) * mm, "construction": true});
            skLineSegment(sketch, "E74.MirrorCS", {"start": v(-7.2, 63.5) * mm, "end": v(-27, 63.5) * mm});
            skLineSegment(sketch, "E75.MirrorCS", {"start": v(-7.2, 69.85) * mm, "end": v(-27, 69.85) * mm});
            skArc(sketch, "E76.MirrorCS", {"start": v(-27, 63.5) * mm, "mid": v(-30.18, 66.68) * mm, "end": v(-27, 69.85) * mm});
            skArc(sketch, "E77.MirrorCS", {"start": v(-7.2, 69.85) * mm, "mid": v(-4.02, 66.68) * mm, "end": v(-7.2, 63.5) * mm});
            skSolve(sketch);
        }
        {
            var Q0;
            Q0 = qSketchRegion(id + "F33", true);
            extrude(context, id + "F34", {"entities" : qUnion([Q0]), "operationType" : NewBodyOperationType.REMOVE, "endBound" : BoundingType.THROUGH_ALL, "oppositeDirection" : true, "depth" : 25.4 * mm});
        }
    });
